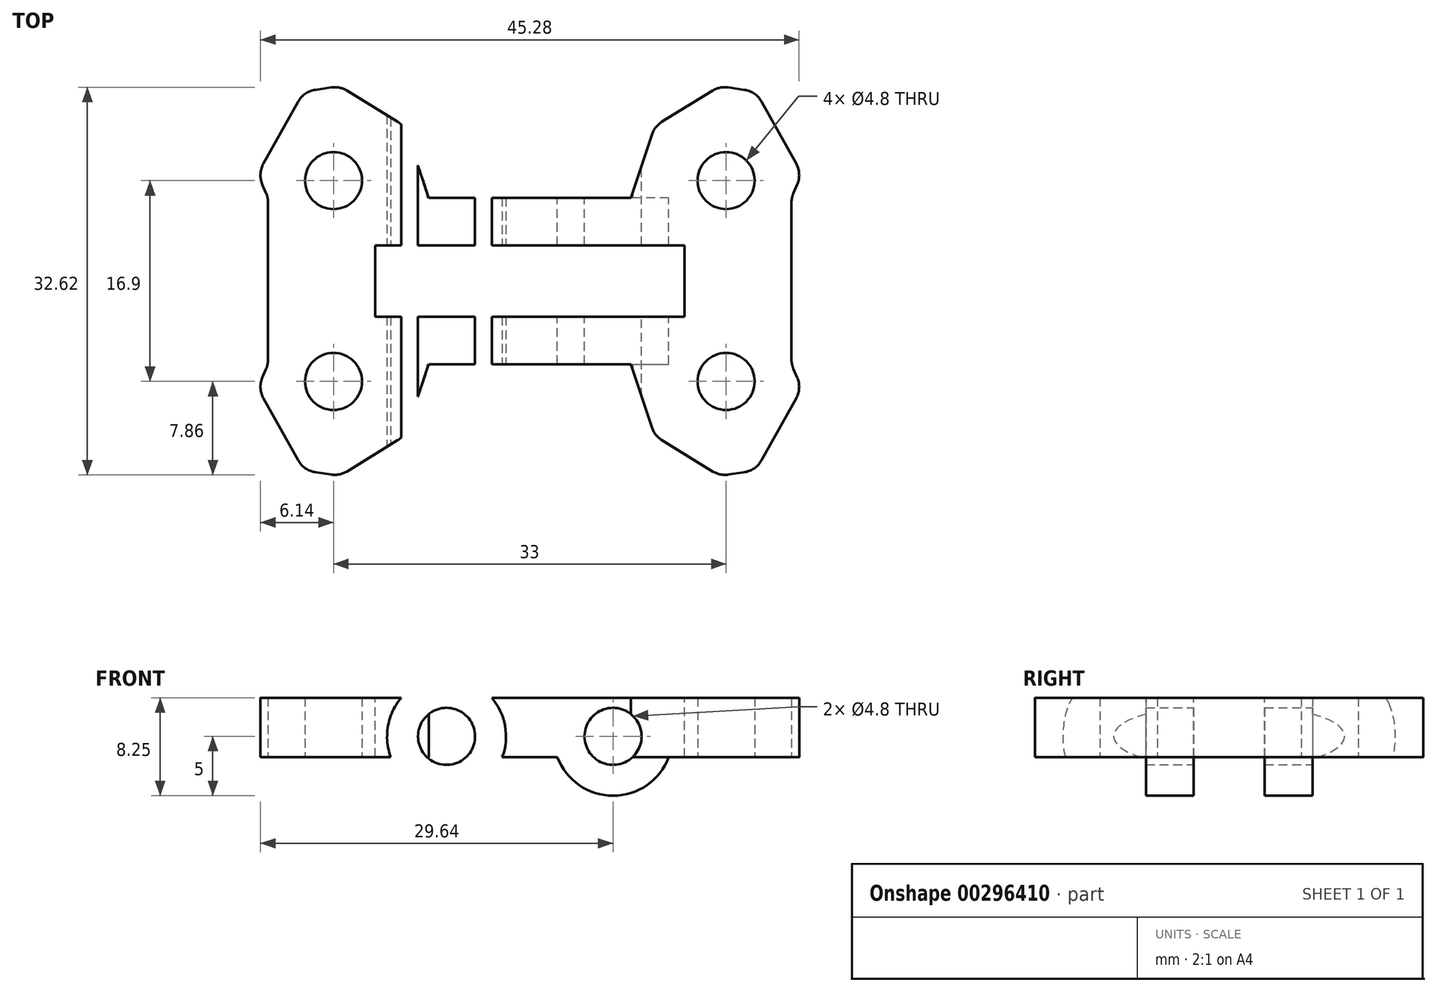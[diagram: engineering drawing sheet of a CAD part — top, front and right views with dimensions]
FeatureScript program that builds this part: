
annotation { "Feature Type Name" : "Feature", "Feature Type Description" : "" }
export const myFeature = defineFeature(function(context is Context, id is Id, definition is map)
    precondition{}
    {
        {
            var Q0;
            Q0=qCreatedBy(makeId("Top.planeOp"),FACE);
            var sketch = newSketch(context, id + "F0", { "sketchPlane" : qUnion([Q0])});
            skLineSegment(sketch, "E0.bottom", {"start": v(16.5, -8.45) * mm, "end": v(-16.5, -8.45) * mm, "construction": true});
            skLineSegment(sketch, "E0.top", {"start": v(16.5, 8.45) * mm, "end": v(-16.5, 8.45) * mm, "construction": true});
            skLineSegment(sketch, "E0.left", {"start": v(16.5, -8.45) * mm, "end": v(16.5, 8.45) * mm, "construction": true});
            skLineSegment(sketch, "E0.right", {"start": v(-16.5, -8.45) * mm, "end": v(-16.5, 8.45) * mm, "construction": true});
            skPoint(sketch, "E0.middle", {"position": v(0, 0) * mm});
            skLineSegment(sketch, "E1", {"start": v(-16.5, 3.75) * mm, "end": v(16.5, 3.75) * mm, "construction": true});
            skLineSegment(sketch, "E2.MirrorCS", {"start": v(-16.5, -3.75) * mm, "end": v(16.5, -3.75) * mm, "construction": true});
            skCircle(sketch, "E3", {"center": v(16.5, 8.45) * mm, "radius": 2.5 * mm, "construction": true});
            skCircle(sketch, "E4", {"center": v(16.5, 8.45) * mm, "radius": 5 * mm, "construction": true});
            skCircle(sketch, "E5.MirrorC", {"center": v(16.5, -8.45) * mm, "radius": 2.5 * mm, "construction": true});
            skCircle(sketch, "E6.MirrorC", {"center": v(16.5, -8.45) * mm, "radius": 5 * mm, "construction": true});
            skCircle(sketch, "E7.MirrorC", {"center": v(-16.5, 8.45) * mm, "radius": 5 * mm, "construction": true});
            skCircle(sketch, "E8.MirrorC", {"center": v(-16.5, 8.45) * mm, "radius": 2.5 * mm, "construction": true});
            skCircle(sketch, "E9.MirrorC", {"center": v(-16.5, -8.45) * mm, "radius": 5 * mm, "construction": true});
            skCircle(sketch, "E10.MirrorC", {"center": v(-16.5, -8.45) * mm, "radius": 2.5 * mm, "construction": true});
            skLineSegment(sketch, "E11", {"start": v(0, 7) * mm, "end": v(8.5, 7) * mm});
            skLineSegment(sketch, "E12", {"start": v(8.5, 7) * mm, "end": v(11.82, 17) * mm});
            skLineSegment(sketch, "E13", {"start": v(11.82, 17) * mm, "end": v(25.45, 15) * mm});
            skLineSegment(sketch, "E14", {"start": v(25.45, 15) * mm, "end": v(22, 7) * mm});
            skLineSegment(sketch, "E15", {"start": v(22, 7) * mm, "end": v(22, 0) * mm});
            skLineSegment(sketch, "E16", {"start": v(22, 0) * mm, "end": v(0, 0) * mm});
            skLineSegment(sketch, "E17", {"start": v(0, 7) * mm, "end": v(0, 0) * mm});
            skCircle(sketch, "E18", {"center": v(16.5, 8.45) * mm, "radius": 2.4 * mm});
            skSolve(sketch);
        }
        {
            var Q0;
            Q0=makeQuery(id+"F0.imprint","IMPRINT",FACE,{"disambiguationData":[TD([[makeQuery(id+"F0.imprint","IMPRINT",EDGE,{"derivedFrom":sQuery(id+"F0.wireOp",EDGE,"E11")}),-1.0]])]});
            extrude(context, id + "F1", {"entities" : qUnion([Q0]), "depth" : 5 * mm, "offsetDistance" : 25 * mm});
        }
        {
            var Q0;
            Q0=makeQuery(id+"F1.opExtrude","SWEPT_BODY",BODY,{"disambiguationData":[OSD([sQuery(id+"F0.wireOp",EDGE,"E11"),sQuery(id+"F0.wireOp",EDGE,"E12"),sQuery(id+"F0.wireOp",EDGE,"E13"),sQuery(id+"F0.wireOp",EDGE,"E14"),sQuery(id+"F0.wireOp",EDGE,"E15"),sQuery(id+"F0.wireOp",EDGE,"E16"),sQuery(id+"F0.wireOp",EDGE,"E17"),sQuery(id+"F0.wireOp",EDGE,"E18")])]});
            var Q1;
            Q1=makeQuery(id+"F1.opExtrude","SWEPT_FACE",FACE,{"disambiguationData":[OSD([sQuery(id+"F0.wireOp",EDGE,"E16")])]});
            mirror(context, id + "F2", {"operationType" : NewBodyOperationType.ADD, "entities" : qUnion([Q0]), "mirrorPlane" : qUnion([Q1])});
        }
        {
            var Q0;
            Q0=makeQuery(id+"F1.opExtrude","SWEPT_BODY",BODY,{"disambiguationData":[OSD([sQuery(id+"F0.wireOp",EDGE,"E11"),sQuery(id+"F0.wireOp",EDGE,"E12"),sQuery(id+"F0.wireOp",EDGE,"E13"),sQuery(id+"F0.wireOp",EDGE,"E14"),sQuery(id+"F0.wireOp",EDGE,"E15"),sQuery(id+"F0.wireOp",EDGE,"E16"),sQuery(id+"F0.wireOp",EDGE,"E17"),sQuery(id+"F0.wireOp",EDGE,"E18")])]});
            var Q1;
            {var subQ0=makeQuery(id+"F1.opExtrude","SWEPT_FACE",FACE,{"disambiguationData":[OSD([sQuery(id+"F0.wireOp",EDGE,"E17")])]});Q1=makeQuery(id+"F2.boolean.opBoolean","MERGE",FACE,{"derivedFrom":[subQ0,makeQuery(id+"F2.opPattern","COPY",FACE,{"derivedFrom":subQ0,"instanceName":"1"})]});}
            mirror(context, id + "F3", {"operationType" : NewBodyOperationType.ADD, "entities" : qUnion([Q0]), "mirrorPlane" : qUnion([Q1])});
        }
        {
            var Q0;
            Q0=makeQuery(id+"F1.opExtrude","SWEPT_EDGE",EDGE,{"disambiguationData":[OSD([sQuery(id+"F0.wireOp",EDGE,"E13"),sQuery(id+"F0.wireOp",EDGE,"E14")])]});
            var Q1;
            Q1=makeQuery(id+"F2.opPattern","COPY",EDGE,{"derivedFrom":makeQuery(id+"F1.opExtrude","SWEPT_EDGE",EDGE,{"disambiguationData":[OSD([sQuery(id+"F0.wireOp",EDGE,"E13"),sQuery(id+"F0.wireOp",EDGE,"E14")])]}),"instanceName":"1"});
            var Q2;
            Q2=makeQuery(id+"F2.opPattern","COPY",EDGE,{"derivedFrom":makeQuery(id+"F1.opExtrude","SWEPT_EDGE",EDGE,{"disambiguationData":[OSD([sQuery(id+"F0.wireOp",EDGE,"E12"),sQuery(id+"F0.wireOp",EDGE,"E13")])]}),"instanceName":"1"});
            var Q3;
            Q3=makeQuery(id+"F3.opPattern","COPY",EDGE,{"derivedFrom":makeQuery(id+"F2.opPattern","COPY",EDGE,{"derivedFrom":makeQuery(id+"F1.opExtrude","SWEPT_EDGE",EDGE,{"disambiguationData":[OSD([sQuery(id+"F0.wireOp",EDGE,"E12"),sQuery(id+"F0.wireOp",EDGE,"E13")])]}),"instanceName":"1"}),"instanceName":"1"});
            var Q4;
            Q4=makeQuery(id+"F3.opPattern","COPY",EDGE,{"derivedFrom":makeQuery(id+"F2.opPattern","COPY",EDGE,{"derivedFrom":makeQuery(id+"F1.opExtrude","SWEPT_EDGE",EDGE,{"disambiguationData":[OSD([sQuery(id+"F0.wireOp",EDGE,"E13"),sQuery(id+"F0.wireOp",EDGE,"E14")])]}),"instanceName":"1"}),"instanceName":"1"});
            var Q5;
            Q5=makeQuery(id+"F3.opPattern","COPY",EDGE,{"derivedFrom":makeQuery(id+"F1.opExtrude","SWEPT_EDGE",EDGE,{"disambiguationData":[OSD([sQuery(id+"F0.wireOp",EDGE,"E13"),sQuery(id+"F0.wireOp",EDGE,"E14")])]}),"instanceName":"1"});
            var Q6;
            Q6=makeQuery(id+"F3.opPattern","COPY",EDGE,{"derivedFrom":makeQuery(id+"F1.opExtrude","SWEPT_EDGE",EDGE,{"disambiguationData":[OSD([sQuery(id+"F0.wireOp",EDGE,"E12"),sQuery(id+"F0.wireOp",EDGE,"E13")])]}),"instanceName":"1"});
            var Q7;
            Q7=makeQuery(id+"F1.opExtrude","SWEPT_EDGE",EDGE,{"disambiguationData":[OSD([sQuery(id+"F0.wireOp",EDGE,"E12"),sQuery(id+"F0.wireOp",EDGE,"E13")])]});
            chamfer(context, id + "F4", {"entities" : qUnion([Q0, Q1, Q2, Q3, Q4, Q5, Q6, Q7]), "width" : 5 * mm, "tangentPropagation" : true});
        }
        {
            var Q0;
            {var subQ0=sQuery(id+"F0.wireOp",EDGE,"E12");Q0=makeQuery(id+"F4.opChamfer","BLEND_EDGE",EDGE,{"blendedFrom":[makeQuery(id+"F1.opExtrude","SWEPT_EDGE",EDGE,{"disambiguationData":[OSD([subQ0,sQuery(id+"F0.wireOp",EDGE,"E13")])]}),makeQuery(id+"F1.opExtrude","SWEPT_FACE",FACE,{"disambiguationData":[OSD([subQ0])]})],"blendedInto":[makeQuery(id+"F1.opExtrude","SWEPT_FACE",FACE,{"disambiguationData":[OSD([subQ0])]})]});}
            var Q1;
            {var subQ0=sQuery(id+"F0.wireOp",EDGE,"E13");Q1=makeQuery(id+"F4.opChamfer","BLEND_EDGE",EDGE,{"blendedFrom":[makeQuery(id+"F1.opExtrude","SWEPT_EDGE",EDGE,{"disambiguationData":[OSD([sQuery(id+"F0.wireOp",EDGE,"E12"),subQ0])]}),makeQuery(id+"F1.opExtrude","SWEPT_FACE",FACE,{"disambiguationData":[OSD([subQ0])]})],"blendedInto":[makeQuery(id+"F1.opExtrude","SWEPT_FACE",FACE,{"disambiguationData":[OSD([subQ0])]})]});}
            var Q2;
            {var subQ0=sQuery(id+"F0.wireOp",EDGE,"E13");Q2=makeQuery(id+"F4.opChamfer","BLEND_EDGE",EDGE,{"blendedFrom":[makeQuery(id+"F1.opExtrude","SWEPT_EDGE",EDGE,{"disambiguationData":[OSD([subQ0,sQuery(id+"F0.wireOp",EDGE,"E14")])]}),makeQuery(id+"F1.opExtrude","SWEPT_FACE",FACE,{"disambiguationData":[OSD([subQ0])]})],"blendedInto":[makeQuery(id+"F1.opExtrude","SWEPT_FACE",FACE,{"disambiguationData":[OSD([subQ0])]})]});}
            var Q3;
            Q3=makeQuery(id+"F1.opExtrude","SWEPT_EDGE",EDGE,{"disambiguationData":[OSD([sQuery(id+"F0.wireOp",EDGE,"E14"),sQuery(id+"F0.wireOp",EDGE,"E15")])]});
            var Q4;
            Q4=makeQuery(id+"F2.opPattern","COPY",EDGE,{"derivedFrom":makeQuery(id+"F1.opExtrude","SWEPT_EDGE",EDGE,{"disambiguationData":[OSD([sQuery(id+"F0.wireOp",EDGE,"E14"),sQuery(id+"F0.wireOp",EDGE,"E15")])]}),"instanceName":"1"});
            var Q5;
            {var subQ0=sQuery(id+"F0.wireOp",EDGE,"E14");Q5=makeQuery(id+"F4.opChamfer","BLEND_EDGE",EDGE,{"blendedFrom":[makeQuery(id+"F2.opPattern","COPY",EDGE,{"derivedFrom":makeQuery(id+"F1.opExtrude","SWEPT_EDGE",EDGE,{"disambiguationData":[OSD([sQuery(id+"F0.wireOp",EDGE,"E13"),subQ0])]}),"instanceName":"1"}),makeQuery(id+"F2.opPattern","COPY",FACE,{"derivedFrom":makeQuery(id+"F1.opExtrude","SWEPT_FACE",FACE,{"disambiguationData":[OSD([subQ0])]}),"instanceName":"1"})],"blendedInto":[makeQuery(id+"F2.opPattern","COPY",FACE,{"derivedFrom":makeQuery(id+"F1.opExtrude","SWEPT_FACE",FACE,{"disambiguationData":[OSD([subQ0])]}),"instanceName":"1"})]});}
            var Q6;
            {var subQ0=sQuery(id+"F0.wireOp",EDGE,"E13");Q6=makeQuery(id+"F4.opChamfer","BLEND_EDGE",EDGE,{"blendedFrom":[makeQuery(id+"F2.opPattern","COPY",EDGE,{"derivedFrom":makeQuery(id+"F1.opExtrude","SWEPT_EDGE",EDGE,{"disambiguationData":[OSD([subQ0,sQuery(id+"F0.wireOp",EDGE,"E14")])]}),"instanceName":"1"}),makeQuery(id+"F2.opPattern","COPY",FACE,{"derivedFrom":makeQuery(id+"F1.opExtrude","SWEPT_FACE",FACE,{"disambiguationData":[OSD([subQ0])]}),"instanceName":"1"})],"blendedInto":[makeQuery(id+"F2.opPattern","COPY",FACE,{"derivedFrom":makeQuery(id+"F1.opExtrude","SWEPT_FACE",FACE,{"disambiguationData":[OSD([subQ0])]}),"instanceName":"1"})]});}
            var Q7;
            {var subQ0=sQuery(id+"F0.wireOp",EDGE,"E13");Q7=makeQuery(id+"F4.opChamfer","BLEND_EDGE",EDGE,{"blendedFrom":[makeQuery(id+"F2.opPattern","COPY",EDGE,{"derivedFrom":makeQuery(id+"F1.opExtrude","SWEPT_EDGE",EDGE,{"disambiguationData":[OSD([sQuery(id+"F0.wireOp",EDGE,"E12"),subQ0])]}),"instanceName":"1"}),makeQuery(id+"F2.opPattern","COPY",FACE,{"derivedFrom":makeQuery(id+"F1.opExtrude","SWEPT_FACE",FACE,{"disambiguationData":[OSD([subQ0])]}),"instanceName":"1"})],"blendedInto":[makeQuery(id+"F2.opPattern","COPY",FACE,{"derivedFrom":makeQuery(id+"F1.opExtrude","SWEPT_FACE",FACE,{"disambiguationData":[OSD([subQ0])]}),"instanceName":"1"})]});}
            var Q8;
            {var subQ0=sQuery(id+"F0.wireOp",EDGE,"E12");Q8=makeQuery(id+"F4.opChamfer","BLEND_EDGE",EDGE,{"blendedFrom":[makeQuery(id+"F2.opPattern","COPY",EDGE,{"derivedFrom":makeQuery(id+"F1.opExtrude","SWEPT_EDGE",EDGE,{"disambiguationData":[OSD([subQ0,sQuery(id+"F0.wireOp",EDGE,"E13")])]}),"instanceName":"1"}),makeQuery(id+"F2.opPattern","COPY",FACE,{"derivedFrom":makeQuery(id+"F1.opExtrude","SWEPT_FACE",FACE,{"disambiguationData":[OSD([subQ0])]}),"instanceName":"1"})],"blendedInto":[makeQuery(id+"F2.opPattern","COPY",FACE,{"derivedFrom":makeQuery(id+"F1.opExtrude","SWEPT_FACE",FACE,{"disambiguationData":[OSD([subQ0])]}),"instanceName":"1"})]});}
            var Q9;
            {var subQ0=sQuery(id+"F0.wireOp",EDGE,"E12");Q9=makeQuery(id+"F4.opChamfer","BLEND_EDGE",EDGE,{"blendedFrom":[makeQuery(id+"F3.opPattern","COPY",EDGE,{"derivedFrom":makeQuery(id+"F2.opPattern","COPY",EDGE,{"derivedFrom":makeQuery(id+"F1.opExtrude","SWEPT_EDGE",EDGE,{"disambiguationData":[OSD([subQ0,sQuery(id+"F0.wireOp",EDGE,"E13")])]}),"instanceName":"1"}),"instanceName":"1"}),makeQuery(id+"F3.opPattern","COPY",FACE,{"derivedFrom":makeQuery(id+"F2.opPattern","COPY",FACE,{"derivedFrom":makeQuery(id+"F1.opExtrude","SWEPT_FACE",FACE,{"disambiguationData":[OSD([subQ0])]}),"instanceName":"1"}),"instanceName":"1"})],"blendedInto":[makeQuery(id+"F3.opPattern","COPY",FACE,{"derivedFrom":makeQuery(id+"F2.opPattern","COPY",FACE,{"derivedFrom":makeQuery(id+"F1.opExtrude","SWEPT_FACE",FACE,{"disambiguationData":[OSD([subQ0])]}),"instanceName":"1"}),"instanceName":"1"})]});}
            var Q10;
            {var subQ0=sQuery(id+"F0.wireOp",EDGE,"E13");Q10=makeQuery(id+"F4.opChamfer","BLEND_EDGE",EDGE,{"blendedFrom":[makeQuery(id+"F3.opPattern","COPY",EDGE,{"derivedFrom":makeQuery(id+"F2.opPattern","COPY",EDGE,{"derivedFrom":makeQuery(id+"F1.opExtrude","SWEPT_EDGE",EDGE,{"disambiguationData":[OSD([sQuery(id+"F0.wireOp",EDGE,"E12"),subQ0])]}),"instanceName":"1"}),"instanceName":"1"}),makeQuery(id+"F3.opPattern","COPY",FACE,{"derivedFrom":makeQuery(id+"F2.opPattern","COPY",FACE,{"derivedFrom":makeQuery(id+"F1.opExtrude","SWEPT_FACE",FACE,{"disambiguationData":[OSD([subQ0])]}),"instanceName":"1"}),"instanceName":"1"})],"blendedInto":[makeQuery(id+"F3.opPattern","COPY",FACE,{"derivedFrom":makeQuery(id+"F2.opPattern","COPY",FACE,{"derivedFrom":makeQuery(id+"F1.opExtrude","SWEPT_FACE",FACE,{"disambiguationData":[OSD([subQ0])]}),"instanceName":"1"}),"instanceName":"1"})]});}
            var Q11;
            {var subQ0=sQuery(id+"F0.wireOp",EDGE,"E13");Q11=makeQuery(id+"F4.opChamfer","BLEND_EDGE",EDGE,{"blendedFrom":[makeQuery(id+"F3.opPattern","COPY",EDGE,{"derivedFrom":makeQuery(id+"F2.opPattern","COPY",EDGE,{"derivedFrom":makeQuery(id+"F1.opExtrude","SWEPT_EDGE",EDGE,{"disambiguationData":[OSD([subQ0,sQuery(id+"F0.wireOp",EDGE,"E14")])]}),"instanceName":"1"}),"instanceName":"1"}),makeQuery(id+"F3.opPattern","COPY",FACE,{"derivedFrom":makeQuery(id+"F2.opPattern","COPY",FACE,{"derivedFrom":makeQuery(id+"F1.opExtrude","SWEPT_FACE",FACE,{"disambiguationData":[OSD([subQ0])]}),"instanceName":"1"}),"instanceName":"1"})],"blendedInto":[makeQuery(id+"F3.opPattern","COPY",FACE,{"derivedFrom":makeQuery(id+"F2.opPattern","COPY",FACE,{"derivedFrom":makeQuery(id+"F1.opExtrude","SWEPT_FACE",FACE,{"disambiguationData":[OSD([subQ0])]}),"instanceName":"1"}),"instanceName":"1"})]});}
            var Q12;
            {var subQ0=sQuery(id+"F0.wireOp",EDGE,"E14");Q12=makeQuery(id+"F4.opChamfer","BLEND_EDGE",EDGE,{"blendedFrom":[makeQuery(id+"F3.opPattern","COPY",EDGE,{"derivedFrom":makeQuery(id+"F2.opPattern","COPY",EDGE,{"derivedFrom":makeQuery(id+"F1.opExtrude","SWEPT_EDGE",EDGE,{"disambiguationData":[OSD([sQuery(id+"F0.wireOp",EDGE,"E13"),subQ0])]}),"instanceName":"1"}),"instanceName":"1"}),makeQuery(id+"F3.opPattern","COPY",FACE,{"derivedFrom":makeQuery(id+"F2.opPattern","COPY",FACE,{"derivedFrom":makeQuery(id+"F1.opExtrude","SWEPT_FACE",FACE,{"disambiguationData":[OSD([subQ0])]}),"instanceName":"1"}),"instanceName":"1"})],"blendedInto":[makeQuery(id+"F3.opPattern","COPY",FACE,{"derivedFrom":makeQuery(id+"F2.opPattern","COPY",FACE,{"derivedFrom":makeQuery(id+"F1.opExtrude","SWEPT_FACE",FACE,{"disambiguationData":[OSD([subQ0])]}),"instanceName":"1"}),"instanceName":"1"})]});}
            var Q13;
            Q13=makeQuery(id+"F3.opPattern","COPY",EDGE,{"derivedFrom":makeQuery(id+"F2.opPattern","COPY",EDGE,{"derivedFrom":makeQuery(id+"F1.opExtrude","SWEPT_EDGE",EDGE,{"disambiguationData":[OSD([sQuery(id+"F0.wireOp",EDGE,"E14"),sQuery(id+"F0.wireOp",EDGE,"E15")])]}),"instanceName":"1"}),"instanceName":"1"});
            var Q14;
            Q14=makeQuery(id+"F3.opPattern","COPY",EDGE,{"derivedFrom":makeQuery(id+"F1.opExtrude","SWEPT_EDGE",EDGE,{"disambiguationData":[OSD([sQuery(id+"F0.wireOp",EDGE,"E14"),sQuery(id+"F0.wireOp",EDGE,"E15")])]}),"instanceName":"1"});
            var Q15;
            {var subQ0=sQuery(id+"F0.wireOp",EDGE,"E14");Q15=makeQuery(id+"F4.opChamfer","BLEND_EDGE",EDGE,{"blendedFrom":[makeQuery(id+"F3.opPattern","COPY",EDGE,{"derivedFrom":makeQuery(id+"F1.opExtrude","SWEPT_EDGE",EDGE,{"disambiguationData":[OSD([sQuery(id+"F0.wireOp",EDGE,"E13"),subQ0])]}),"instanceName":"1"}),makeQuery(id+"F3.opPattern","COPY",FACE,{"derivedFrom":makeQuery(id+"F1.opExtrude","SWEPT_FACE",FACE,{"disambiguationData":[OSD([subQ0])]}),"instanceName":"1"})],"blendedInto":[makeQuery(id+"F3.opPattern","COPY",FACE,{"derivedFrom":makeQuery(id+"F1.opExtrude","SWEPT_FACE",FACE,{"disambiguationData":[OSD([subQ0])]}),"instanceName":"1"})]});}
            var Q16;
            {var subQ0=sQuery(id+"F0.wireOp",EDGE,"E13");Q16=makeQuery(id+"F4.opChamfer","BLEND_EDGE",EDGE,{"blendedFrom":[makeQuery(id+"F3.opPattern","COPY",EDGE,{"derivedFrom":makeQuery(id+"F1.opExtrude","SWEPT_EDGE",EDGE,{"disambiguationData":[OSD([subQ0,sQuery(id+"F0.wireOp",EDGE,"E14")])]}),"instanceName":"1"}),makeQuery(id+"F3.opPattern","COPY",FACE,{"derivedFrom":makeQuery(id+"F1.opExtrude","SWEPT_FACE",FACE,{"disambiguationData":[OSD([subQ0])]}),"instanceName":"1"})],"blendedInto":[makeQuery(id+"F3.opPattern","COPY",FACE,{"derivedFrom":makeQuery(id+"F1.opExtrude","SWEPT_FACE",FACE,{"disambiguationData":[OSD([subQ0])]}),"instanceName":"1"})]});}
            var Q17;
            {var subQ0=sQuery(id+"F0.wireOp",EDGE,"E12");Q17=makeQuery(id+"F4.opChamfer","BLEND_EDGE",EDGE,{"blendedFrom":[makeQuery(id+"F3.opPattern","COPY",EDGE,{"derivedFrom":makeQuery(id+"F1.opExtrude","SWEPT_EDGE",EDGE,{"disambiguationData":[OSD([subQ0,sQuery(id+"F0.wireOp",EDGE,"E13")])]}),"instanceName":"1"}),makeQuery(id+"F3.opPattern","COPY",FACE,{"derivedFrom":makeQuery(id+"F1.opExtrude","SWEPT_FACE",FACE,{"disambiguationData":[OSD([subQ0])]}),"instanceName":"1"})],"blendedInto":[makeQuery(id+"F3.opPattern","COPY",FACE,{"derivedFrom":makeQuery(id+"F1.opExtrude","SWEPT_FACE",FACE,{"disambiguationData":[OSD([subQ0])]}),"instanceName":"1"})]});}
            var Q18;
            {var subQ0=sQuery(id+"F0.wireOp",EDGE,"E14");Q18=makeQuery(id+"F4.opChamfer","BLEND_EDGE",EDGE,{"blendedFrom":[makeQuery(id+"F1.opExtrude","SWEPT_EDGE",EDGE,{"disambiguationData":[OSD([sQuery(id+"F0.wireOp",EDGE,"E13"),subQ0])]}),makeQuery(id+"F1.opExtrude","SWEPT_FACE",FACE,{"disambiguationData":[OSD([subQ0])]})],"blendedInto":[makeQuery(id+"F1.opExtrude","SWEPT_FACE",FACE,{"disambiguationData":[OSD([subQ0])]})]});}
            var Q19;
            {var subQ0=sQuery(id+"F0.wireOp",EDGE,"E13");Q19=makeQuery(id+"F4.opChamfer","BLEND_EDGE",EDGE,{"blendedFrom":[makeQuery(id+"F3.opPattern","COPY",EDGE,{"derivedFrom":makeQuery(id+"F1.opExtrude","SWEPT_EDGE",EDGE,{"disambiguationData":[OSD([sQuery(id+"F0.wireOp",EDGE,"E12"),subQ0])]}),"instanceName":"1"}),makeQuery(id+"F3.opPattern","COPY",FACE,{"derivedFrom":makeQuery(id+"F1.opExtrude","SWEPT_FACE",FACE,{"disambiguationData":[OSD([subQ0])]}),"instanceName":"1"})],"blendedInto":[makeQuery(id+"F3.opPattern","COPY",FACE,{"derivedFrom":makeQuery(id+"F1.opExtrude","SWEPT_FACE",FACE,{"disambiguationData":[OSD([subQ0])]}),"instanceName":"1"})]});}
            fillet(context, id + "F5", {"entities" : qUnion([Q0, Q1, Q2, Q3, Q4, Q5, Q6, Q7, Q8, Q9, Q10, Q11, Q12, Q13, Q14, Q15, Q16, Q17, Q18, Q19]), "radius" : 2 * mm, "tangentPropagation" : true, "allowEdgeOverflow" : false});
        }
        {
            var Q0;
            Q0=qCreatedBy(makeId("Front.planeOp"),FACE);
            var sketch = newSketch(context, id + "F6", { "sketchPlane" : qUnion([Q0])});
            skLineSegment(sketch, "E19", {"start": v(-8.97, 10.5) * mm, "end": v(24.05, 10.5) * mm, "construction": true});
            skLineSegment(sketch, "E20", {"start": v(-11.27, 6.75) * mm, "end": v(33.83, 6.75) * mm, "construction": true});
            skLineSegment(sketch, "E21.MirrorCS", {"start": v(-11.27, 14.25) * mm, "end": v(33.83, 14.25) * mm, "construction": true});
            skLineSegment(sketch, "E22", {"start": v(7, -11.15) * mm, "end": v(7, 31.86) * mm, "construction": true});
            skCircle(sketch, "E23", {"center": v(7, 1.75) * mm, "radius": 5 * mm});
            skCircle(sketch, "E24", {"center": v(7, 1.75) * mm, "radius": 2.4 * mm});
            skLineSegment(sketch, "E25", {"start": v(3.2, 5) * mm, "end": v(10.8, 5) * mm});
            skCircle(sketch, "E26.MirrorC", {"center": v(-7, 1.75) * mm, "radius": 2.4 * mm});
            skCircle(sketch, "E27.MirrorC", {"center": v(-7, 1.75) * mm, "radius": 5 * mm});
            skLineSegment(sketch, "E28.MirrorCS", {"start": v(-3.2, 5) * mm, "end": v(-10.8, 5) * mm});
            skSolve(sketch);
        }
        {
            var Q0;
            Q0=makeQuery(id+"F6.imprint","IMPRINT",FACE,{"disambiguationData":[TD([[makeQuery(id+"F6.imprint","IMPRINT",EDGE,{"derivedFrom":sQuery(id+"F6.wireOp",EDGE,"E24")}),-1.0]])]});
            var Q1;
            Q1=makeQuery(id+"F6.imprint","IMPRINT",FACE,{"disambiguationData":[TD([[makeQuery(id+"F6.imprint","IMPRINT",EDGE,{"derivedFrom":sQuery(id+"F6.wireOp",EDGE,"E26.MirrorC")}),1.0]])]});
            var Q2;
            {var subQ0=makeQuery(id+"F2.opPattern","COPY",FACE,{"derivedFrom":makeQuery(id+"F1.opExtrude","SWEPT_FACE",FACE,{"disambiguationData":[OSD([sQuery(id+"F0.wireOp",EDGE,"E11")])]}),"instanceName":"1"});Q2=makeQuery(id+"F3.boolean.opBoolean","MERGE",FACE,{"derivedFrom":[subQ0,makeQuery(id+"F3.opPattern","COPY",FACE,{"derivedFrom":subQ0,"instanceName":"1"})]});}
            var Q3;
            {var subQ0=makeQuery(id+"F1.opExtrude","SWEPT_FACE",FACE,{"disambiguationData":[OSD([sQuery(id+"F0.wireOp",EDGE,"E11")])]});Q3=makeQuery(id+"F3.boolean.opBoolean","MERGE",FACE,{"derivedFrom":[subQ0,makeQuery(id+"F3.opPattern","COPY",FACE,{"derivedFrom":subQ0,"instanceName":"1"})]});}
            extrude(context, id + "F7", {"entities" : qUnion([Q0, Q1]), "operationType" : NewBodyOperationType.ADD, "endBound" : BoundingType.UP_TO_SURFACE, "depth" : 25 * mm, "endBoundEntityFace" : qUnion([Q2]), "offsetDistance" : 25 * mm, "hasSecondDirection" : true, "secondDirectionBound" : BoundingType.UP_TO_SURFACE, "secondDirectionOppositeDirection" : true, "secondDirectionDepth" : 25 * mm, "secondDirectionBoundEntityFace" : qUnion([Q3])});
        }
        {
            var Q0;
            Q0=makeQuery(id+"F6.imprint","IMPRINT",FACE,{"disambiguationData":[TD([[makeQuery(id+"F6.imprint","IMPRINT",EDGE,{"derivedFrom":sQuery(id+"F6.wireOp",EDGE,"E24")}),1.0]])]});
            var Q1;
            Q1=makeQuery(id+"F6.imprint","IMPRINT",FACE,{"disambiguationData":[TD([[makeQuery(id+"F6.imprint","IMPRINT",EDGE,{"derivedFrom":sQuery(id+"F6.wireOp",EDGE,"E26.MirrorC")}),-1.0]])]});
            extrude(context, id + "F8", {"entities" : qUnion([Q0, Q1]), "operationType" : NewBodyOperationType.REMOVE, "endBound" : BoundingType.THROUGH_ALL, "oppositeDirection" : true, "depth" : 25 * mm, "offsetDistance" : 25 * mm, "hasSecondDirection" : true, "secondDirectionBound" : BoundingType.THROUGH_ALL, "secondDirectionOppositeDirection" : false, "secondDirectionDepth" : 25 * mm});
        }
        {
            var Q0;
            {var subQ0=makeQuery(id+"F1.opExtrude","CAP_FACE",FACE,{"disambiguationData":[OSD([sQuery(id+"F0.wireOp",EDGE,"E11"),sQuery(id+"F0.wireOp",EDGE,"E12"),sQuery(id+"F0.wireOp",EDGE,"E13"),sQuery(id+"F0.wireOp",EDGE,"E14"),sQuery(id+"F0.wireOp",EDGE,"E15"),sQuery(id+"F0.wireOp",EDGE,"E16"),sQuery(id+"F0.wireOp",EDGE,"E17"),sQuery(id+"F0.wireOp",EDGE,"E18")])],"isStart":false});var subQ1=makeQuery(id+"F2.boolean.opBoolean","MERGE",FACE,{"derivedFrom":[subQ0,makeQuery(id+"F2.opPattern","COPY",FACE,{"derivedFrom":subQ0,"instanceName":"1"})]});Q0=makeQuery(id+"F3.boolean.opBoolean","MERGE",FACE,{"derivedFrom":[subQ1,makeQuery(id+"F3.opPattern","COPY",FACE,{"derivedFrom":subQ1,"instanceName":"1"})]});}
            var sketch = newSketch(context, id + "F9", { "sketchPlane" : qUnion([Q0])});
            skLineSegment(sketch, "E29.bottom", {"start": v(13, -3) * mm, "end": v(-13, -3) * mm});
            skLineSegment(sketch, "E29.top", {"start": v(13, 3) * mm, "end": v(-13, 3) * mm});
            skLineSegment(sketch, "E29.left", {"start": v(13, -3) * mm, "end": v(13, 3) * mm});
            skLineSegment(sketch, "E29.right", {"start": v(-13, -3) * mm, "end": v(-13, 3) * mm});
            skPoint(sketch, "E29.middle", {"position": v(0, 0) * mm});
            skSolve(sketch);
        }
        {
            var Q0;
            Q0=makeQuery(id+"F9.imprint","IMPRINT",FACE,{"disambiguationData":[TD([[makeQuery(id+"F9.imprint","IMPRINT",EDGE,{"derivedFrom":sQuery(id+"F9.wireOp",EDGE,"E29.bottom")}),-1.0]])]});
            extrude(context, id + "F10", {"entities" : qUnion([Q0]), "operationType" : NewBodyOperationType.REMOVE, "endBound" : BoundingType.THROUGH_ALL, "oppositeDirection" : true, "depth" : 25 * mm, "offsetDistance" : 25 * mm});
        }
    });
